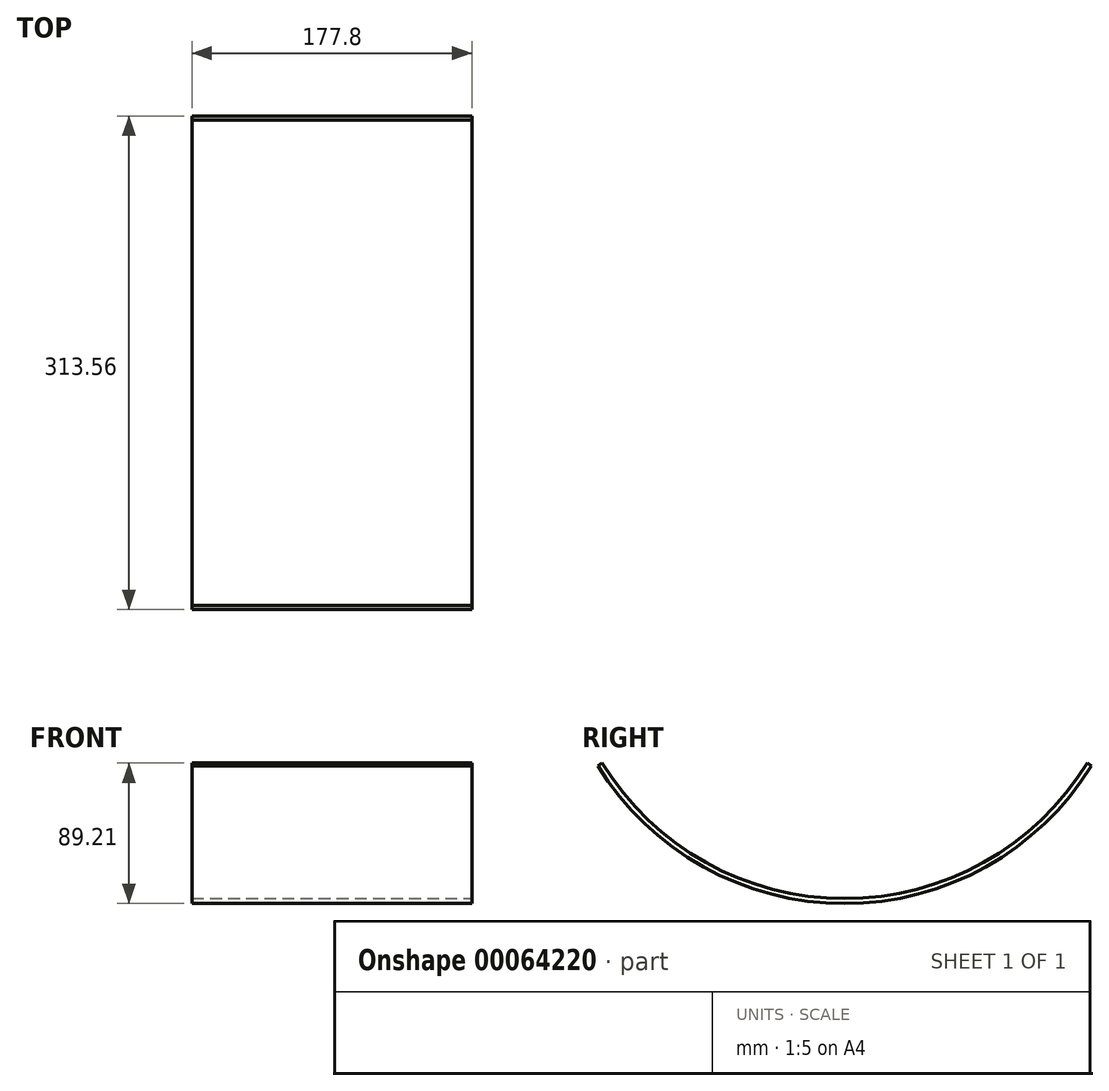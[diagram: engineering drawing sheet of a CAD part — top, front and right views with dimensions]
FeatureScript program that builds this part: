
annotation { "Feature Type Name" : "Feature", "Feature Type Description" : "" }
export const myFeature = defineFeature(function(context is Context, id is Id, definition is map)
    precondition{}
    {
        {
            var Q0;
            Q0=qCreatedBy(makeId("Right.planeOp"),FACE);
            var sketch = newSketch(context, id + "F0", { "sketchPlane" : qUnion([Q0])});
            skArc(sketch, "E0", {"start": v(156.78, -96.6) * mm, "mid": v(0, -184.15) * mm, "end": v(-156.78, -96.6) * mm});
            skArc(sketch, "E1.0", {"start": v(154.07, -94.94) * mm, "mid": v(0, -180.98) * mm, "end": v(-154.07, -94.94) * mm});
            skLineSegment(sketch, "E2", {"start": v(154.07, -94.94) * mm, "end": v(156.78, -96.6) * mm});
            skLineSegment(sketch, "E3", {"start": v(-156.78, -96.6) * mm, "end": v(-154.07, -94.94) * mm});
            skSolve(sketch);
        }
        {
            var Q0;
            Q0 = qSketchRegion(id + "F0", true);
            extrude(context, id + "F1", {"entities" : qUnion([Q0]), "endBound" : BoundingType.SYMMETRIC, "oppositeDirection" : true, "depth" : 177.8 * mm});
        }
    });
